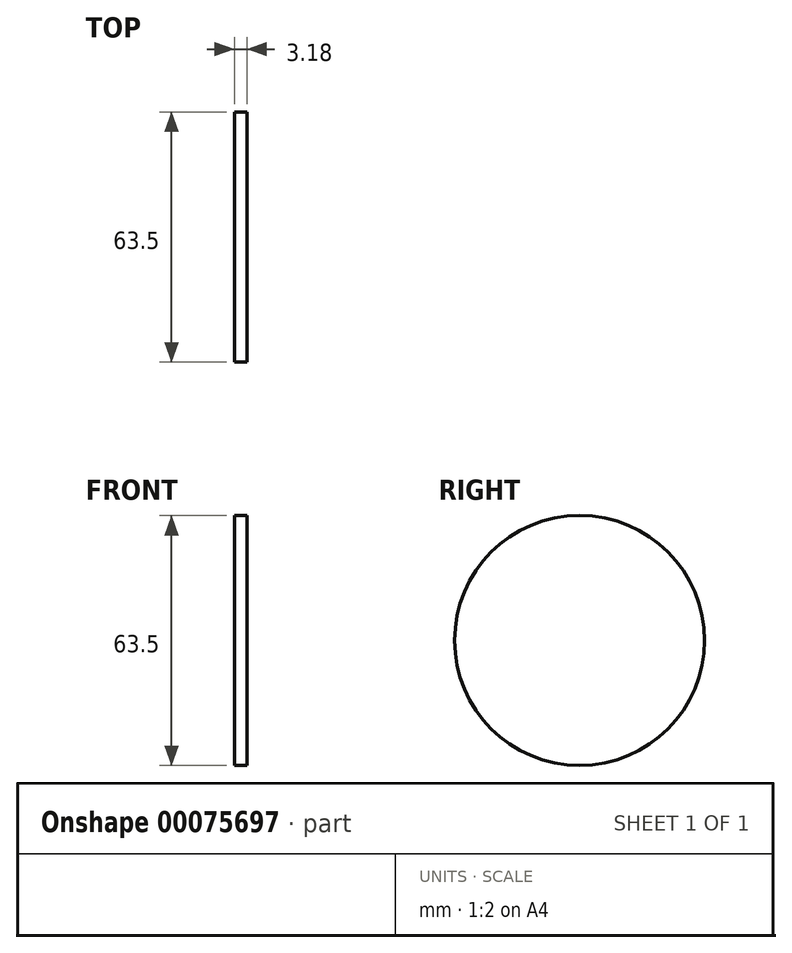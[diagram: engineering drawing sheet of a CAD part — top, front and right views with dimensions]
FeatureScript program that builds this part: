
annotation { "Feature Type Name" : "Feature", "Feature Type Description" : "" }
export const myFeature = defineFeature(function(context is Context, id is Id, definition is map)
    precondition{}
    {
        {
            var Q0;
            Q0=qCreatedBy(makeId("Right.planeOp"),FACE);
            var sketch = newSketch(context, id + "F0", { "sketchPlane" : qUnion([Q0])});
            skCircle(sketch, "E0", {"center": v(0, 0) * mm, "radius": 31.75 * mm});
            skSolve(sketch);
        }
        {
            var Q0;
            Q0 = qSketchRegion(id + "F0", true);
            extrude(context, id + "F1", {"entities" : qUnion([Q0]), "depth" : 3.17 * mm});
        }
    });
